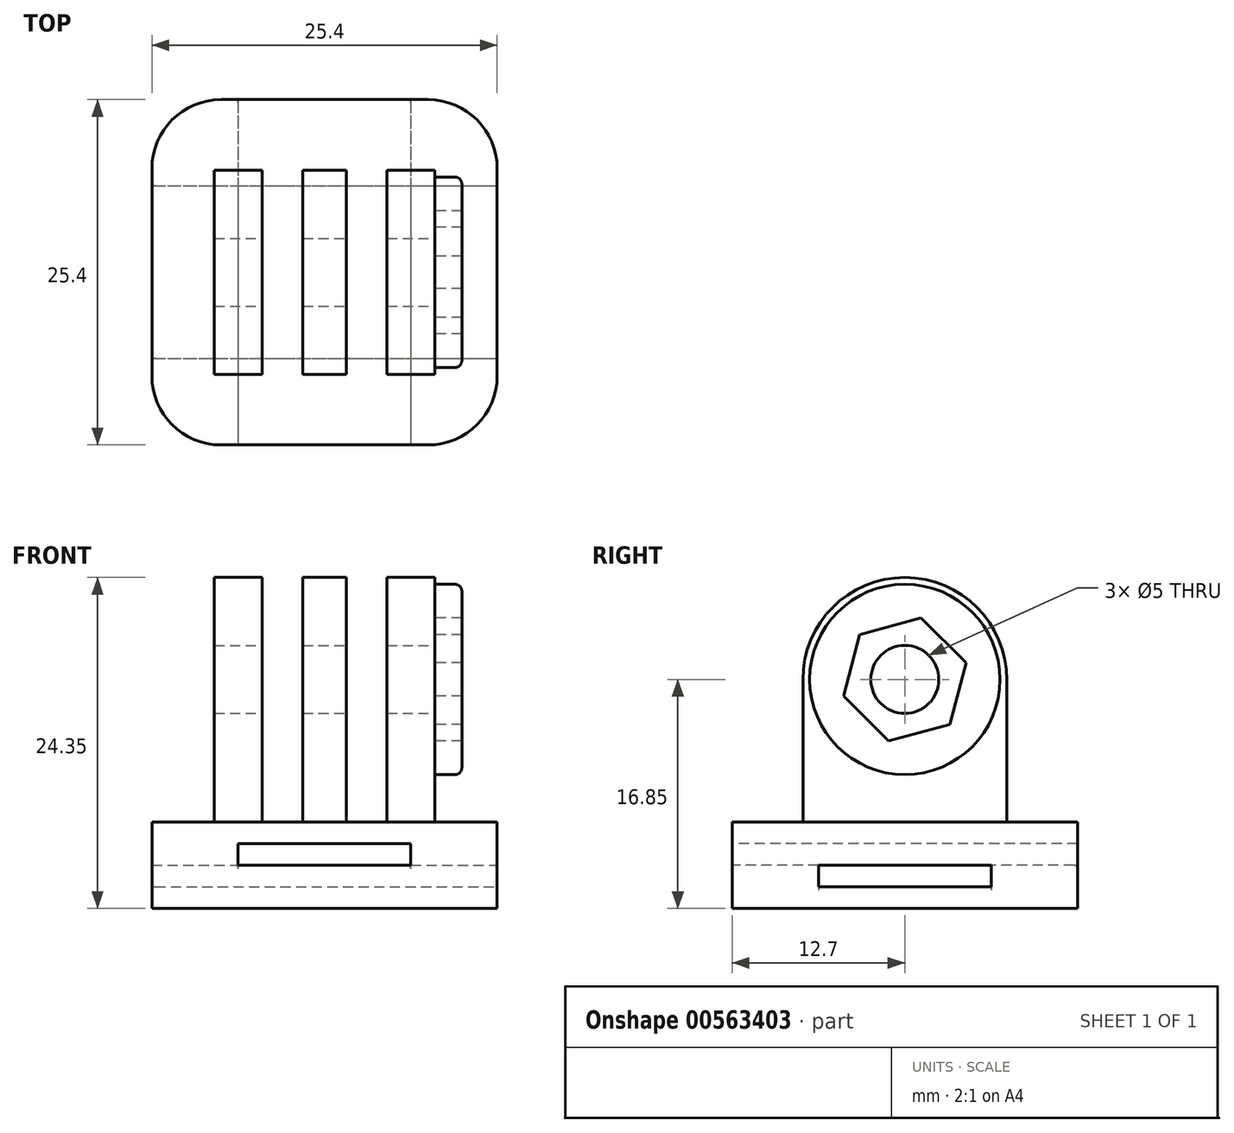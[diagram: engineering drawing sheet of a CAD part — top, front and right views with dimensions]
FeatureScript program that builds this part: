
annotation { "Feature Type Name" : "Feature", "Feature Type Description" : "" }
export const myFeature = defineFeature(function(context is Context, id is Id, definition is map)
    precondition{}
    {
        {
            var Q0;
            Q0=qCreatedBy(makeId("Top.planeOp"),FACE);
            var sketch = newSketch(context, id + "F0", { "sketchPlane" : qUnion([Q0])});
            skLineSegment(sketch, "E0.bottom", {"start": v(-12.7, 12.7) * mm, "end": v(12.7, 12.7) * mm});
            skLineSegment(sketch, "E0.top", {"start": v(-12.7, -12.7) * mm, "end": v(12.7, -12.7) * mm});
            skLineSegment(sketch, "E0.left", {"start": v(-12.7, 12.7) * mm, "end": v(-12.7, -12.7) * mm});
            skLineSegment(sketch, "E0.right", {"start": v(12.7, 12.7) * mm, "end": v(12.7, -12.7) * mm});
            skPoint(sketch, "E0.middle", {"position": v(0, 0) * mm});
            skSolve(sketch);
        }
        {
            var Q0;
            Q0=makeQuery(id+"F0.imprint","IMPRINT",FACE,{"disambiguationData":[TD([[makeQuery(id+"F0.imprint","IMPRINT",EDGE,{"derivedFrom":sQuery(id+"F0.wireOp",EDGE,"E0.bottom")}),-1.0]])]});
            extrude(context, id + "F1", {"entities" : qUnion([Q0]), "depth" : 6.35 * mm, "offsetDistance" : 25.4 * mm});
        }
        {
            var Q0;
            Q0=makeQuery(id+"F1.opExtrude","SWEPT_FACE",FACE,{"disambiguationData":[OSD([sQuery(id+"F0.wireOp",EDGE,"E0.right")])]});
            var sketch = newSketch(context, id + "F2", { "sketchPlane" : qUnion([Q0])});
            skLineSegment(sketch, "E1.bottom", {"start": v(-6.35, 3.17) * mm, "end": v(6.35, 3.18) * mm});
            skLineSegment(sketch, "E1.top", {"start": v(-6.35, 1.59) * mm, "end": v(6.35, 1.59) * mm});
            skLineSegment(sketch, "E1.left", {"start": v(-6.35, 3.17) * mm, "end": v(-6.35, 1.59) * mm});
            skLineSegment(sketch, "E1.right", {"start": v(6.35, 3.18) * mm, "end": v(6.35, 1.59) * mm});
            skPoint(sketch, "E1.middle", {"position": v(0, 2.38) * mm});
            skSolve(sketch);
        }
        {
            var Q0;
            Q0=makeQuery(id+"F2.imprint","IMPRINT",FACE,{"disambiguationData":[TD([[makeQuery(id+"F2.imprint","IMPRINT",EDGE,{"derivedFrom":sQuery(id+"F2.wireOp",EDGE,"E1.bottom")}),-1.0]])]});
            extrude(context, id + "F3", {"entities" : qUnion([Q0]), "operationType" : NewBodyOperationType.REMOVE, "endBound" : BoundingType.THROUGH_ALL, "oppositeDirection" : true, "depth" : 25.4 * mm, "offsetDistance" : 25.4 * mm});
        }
        {
            var Q0;
            Q0=makeQuery(id+"F1.opExtrude","SWEPT_FACE",FACE,{"disambiguationData":[OSD([sQuery(id+"F0.wireOp",EDGE,"E0.top")])]});
            var sketch = newSketch(context, id + "F4", { "sketchPlane" : qUnion([Q0])});
            skLineSegment(sketch, "E2.bottom", {"start": v(-6.35, 4.76) * mm, "end": v(6.35, 4.76) * mm});
            skLineSegment(sketch, "E2.top", {"start": v(-6.35, 3.17) * mm, "end": v(6.35, 3.17) * mm});
            skLineSegment(sketch, "E2.left", {"start": v(-6.35, 4.76) * mm, "end": v(-6.35, 3.17) * mm});
            skLineSegment(sketch, "E2.right", {"start": v(6.35, 4.76) * mm, "end": v(6.35, 3.17) * mm});
            skPoint(sketch, "E2.middle", {"position": v(0, 3.97) * mm});
            skSolve(sketch);
        }
        {
            var Q0;
            Q0=makeQuery(id+"F4.imprint","IMPRINT",FACE,{"disambiguationData":[TD([[makeQuery(id+"F4.imprint","IMPRINT",EDGE,{"derivedFrom":sQuery(id+"F4.wireOp",EDGE,"E2.bottom")}),-1.0]])]});
            extrude(context, id + "F5", {"entities" : qUnion([Q0]), "operationType" : NewBodyOperationType.REMOVE, "endBound" : BoundingType.THROUGH_ALL, "oppositeDirection" : true, "depth" : 25.4 * mm, "offsetDistance" : 25.4 * mm});
        }
        {
            var Q0;
            Q0=makeQuery(id+"F1.opExtrude","CAP_FACE",FACE,{"disambiguationData":[OSD([sQuery(id+"F0.wireOp",EDGE,"E0.bottom"),sQuery(id+"F0.wireOp",EDGE,"E0.top"),sQuery(id+"F0.wireOp",EDGE,"E0.left"),sQuery(id+"F0.wireOp",EDGE,"E0.right")])],"isStart":false});
            var sketch = newSketch(context, id + "F6", { "sketchPlane" : qUnion([Q0])});
            skLineSegment(sketch, "E3.bottom", {"start": v(-1.6, 7.5) * mm, "end": v(1.6, 7.5) * mm});
            skLineSegment(sketch, "E3.top", {"start": v(-1.6, -7.5) * mm, "end": v(1.6, -7.5) * mm});
            skLineSegment(sketch, "E3.left", {"start": v(-1.6, 7.5) * mm, "end": v(-1.6, -7.5) * mm});
            skLineSegment(sketch, "E3.right", {"start": v(1.6, 7.5) * mm, "end": v(1.6, -7.5) * mm});
            skPoint(sketch, "E3.middle", {"position": v(0, 0) * mm});
            skLineSegment(sketch, "E4.bottom", {"start": v(4.6, 7.5) * mm, "end": v(8.1, 7.5) * mm});
            skLineSegment(sketch, "E4.top", {"start": v(4.6, -7.5) * mm, "end": v(8.1, -7.5) * mm});
            skLineSegment(sketch, "E4.left", {"start": v(4.6, 7.5) * mm, "end": v(4.6, -7.5) * mm});
            skLineSegment(sketch, "E4.right", {"start": v(8.1, 7.5) * mm, "end": v(8.1, -7.5) * mm});
            skPoint(sketch, "E4.middle", {"position": v(6.35, 0) * mm});
            skLineSegment(sketch, "E5.MirrorCS", {"start": v(-4.6, 7.5) * mm, "end": v(-4.6, -7.5) * mm});
            skLineSegment(sketch, "E6.MirrorCS", {"start": v(-4.6, 7.5) * mm, "end": v(-8.1, 7.5) * mm});
            skLineSegment(sketch, "E7.MirrorCS", {"start": v(-8.1, 7.5) * mm, "end": v(-8.1, -7.5) * mm});
            skLineSegment(sketch, "E8.MirrorCS", {"start": v(-4.6, -7.5) * mm, "end": v(-8.1, -7.5) * mm});
            skSolve(sketch);
        }
        {
            var Q0;
            Q0=makeQuery(id+"F6.imprint","IMPRINT",FACE,{"disambiguationData":[TD([[makeQuery(id+"F6.imprint","IMPRINT",EDGE,{"derivedFrom":sQuery(id+"F6.wireOp",EDGE,"E5.MirrorCS")}),-1.0]])]});
            var Q1;
            Q1=makeQuery(id+"F6.imprint","IMPRINT",FACE,{"disambiguationData":[TD([[makeQuery(id+"F6.imprint","IMPRINT",EDGE,{"derivedFrom":sQuery(id+"F6.wireOp",EDGE,"E3.bottom")}),-1.0]])]});
            var Q2;
            Q2=makeQuery(id+"F6.imprint","IMPRINT",FACE,{"disambiguationData":[TD([[makeQuery(id+"F6.imprint","IMPRINT",EDGE,{"derivedFrom":sQuery(id+"F6.wireOp",EDGE,"E4.bottom")}),-1.0]])]});
            extrude(context, id + "F7", {"entities" : qUnion([Q0, Q1, Q2]), "operationType" : NewBodyOperationType.ADD, "depth" : 18 * mm, "offsetDistance" : 25.4 * mm});
        }
        {
            var Q0;
            Q0=makeQuery(id+"F7.opExtrude","CAP_EDGE",EDGE,{"disambiguationData":[OSD([sQuery(id+"F6.wireOp",EDGE,"E4.top")])],"isStart":false});
            var Q1;
            Q1=makeQuery(id+"F7.opExtrude","CAP_EDGE",EDGE,{"disambiguationData":[OSD([sQuery(id+"F6.wireOp",EDGE,"E3.top")])],"isStart":false});
            var Q2;
            Q2=makeQuery(id+"F7.opExtrude","CAP_EDGE",EDGE,{"disambiguationData":[OSD([sQuery(id+"F6.wireOp",EDGE,"E8.MirrorCS")])],"isStart":false});
            var Q3;
            Q3=makeQuery(id+"F7.opExtrude","CAP_EDGE",EDGE,{"disambiguationData":[OSD([sQuery(id+"F6.wireOp",EDGE,"E6.MirrorCS")])],"isStart":false});
            var Q4;
            Q4=makeQuery(id+"F7.opExtrude","CAP_EDGE",EDGE,{"disambiguationData":[OSD([sQuery(id+"F6.wireOp",EDGE,"E4.bottom")])],"isStart":false});
            var Q5;
            Q5=makeQuery(id+"F7.opExtrude","CAP_EDGE",EDGE,{"disambiguationData":[OSD([sQuery(id+"F6.wireOp",EDGE,"E3.bottom")])],"isStart":false});
            fillet(context, id + "F8", {"entities" : qUnion([Q0, Q1, Q2, Q3, Q4, Q5]), "radius" : 7.5 * mm, "tangentPropagation" : true, "allowEdgeOverflow" : false});
        }
        {
            var Q0;
            Q0=makeQuery(id+"F1.opExtrude","SWEPT_EDGE",EDGE,{"disambiguationData":[OSD([sQuery(id+"F0.wireOp",EDGE,"E0.bottom"),sQuery(id+"F0.wireOp",EDGE,"E0.right")])]});
            var Q1;
            Q1=makeQuery(id+"F1.opExtrude","SWEPT_EDGE",EDGE,{"disambiguationData":[OSD([sQuery(id+"F0.wireOp",EDGE,"E0.top"),sQuery(id+"F0.wireOp",EDGE,"E0.right")])]});
            var Q2;
            Q2=makeQuery(id+"F1.opExtrude","SWEPT_EDGE",EDGE,{"disambiguationData":[OSD([sQuery(id+"F0.wireOp",EDGE,"E0.bottom"),sQuery(id+"F0.wireOp",EDGE,"E0.left")])]});
            var Q3;
            Q3=makeQuery(id+"F1.opExtrude","SWEPT_EDGE",EDGE,{"disambiguationData":[OSD([sQuery(id+"F0.wireOp",EDGE,"E0.top"),sQuery(id+"F0.wireOp",EDGE,"E0.left")])]});
            fillet(context, id + "F9", {"entities" : qUnion([Q0, Q1, Q2, Q3]), "radius" : 5.08 * mm, "tangentPropagation" : true, "allowEdgeOverflow" : false});
        }
        {
            var Q0;
            Q0=makeQuery(id+"F7.opExtrude","SWEPT_FACE",FACE,{"disambiguationData":[OSD([sQuery(id+"F6.wireOp",EDGE,"E4.right")])]});
            var sketch = newSketch(context, id + "F10", { "sketchPlane" : qUnion([Q0])});
            skPoint(sketch, "E9", {"position": v(0, 16.85) * mm});
            skCircle(sketch, "E10.cCircle", {"center": v(0, 16.85) * mm, "radius": 4.68 * mm, "construction": true});
            skLineSegment(sketch, "E10.0", {"start": v(-3.32, 20.15) * mm, "end": v(1.2, 21.37) * mm});
            skLineSegment(sketch, "E10.1", {"start": v(1.2, 21.37) * mm, "end": v(4.51, 18.07) * mm});
            skLineSegment(sketch, "E10.2", {"start": v(4.51, 18.07) * mm, "end": v(3.32, 13.55) * mm});
            skLineSegment(sketch, "E10.3", {"start": v(3.32, 13.55) * mm, "end": v(-1.2, 12.33) * mm});
            skLineSegment(sketch, "E10.4", {"start": v(-1.2, 12.33) * mm, "end": v(-4.51, 15.63) * mm});
            skLineSegment(sketch, "E10.5", {"start": v(-4.51, 15.63) * mm, "end": v(-3.32, 20.15) * mm});
            skCircle(sketch, "E11", {"center": v(0, 16.85) * mm, "radius": 7 * mm});
            skSolve(sketch);
        }
        {
            var Q0;
            Q0=makeQuery(id+"F10.imprint","IMPRINT",FACE,{"disambiguationData":[TD([[makeQuery(id+"F10.imprint","IMPRINT",EDGE,{"derivedFrom":sQuery(id+"F10.wireOp",EDGE,"E10.0")}),1.0]])]});
            extrude(context, id + "F11", {"entities" : qUnion([Q0]), "operationType" : NewBodyOperationType.ADD, "depth" : 2 * mm, "offsetDistance" : 25.4 * mm});
        }
        {
            var Q0;
            Q0=sQuery(id+"F10.wireOp",VERTEX,"E9");
            var Q1;
            Q1=makeQuery(id+"F1.opExtrude","SWEPT_BODY",BODY,{"disambiguationData":[OSD([sQuery(id+"F0.wireOp",EDGE,"E0.bottom"),sQuery(id+"F0.wireOp",EDGE,"E0.top"),sQuery(id+"F0.wireOp",EDGE,"E0.left"),sQuery(id+"F0.wireOp",EDGE,"E0.right")])]});
            hole(context, id + "F12", {"style" : HoleStyle.SIMPLE, "endStyle" : HoleEndStyle.THROUGH, "holeDiameter" : 5 * mm, "majorDiameter" : 6.35 * mm, "isTappedThrough" : true, "tappedDepth" : 12.7 * mm, "tapClearance" : 3, "locations" : qUnion([Q0]), "scope" : qUnion([Q1])});
        }
        {
            var Q0;
            Q0=makeQuery(id+"F11.opExtrude","CAP_EDGE",EDGE,{"disambiguationData":[OSD([sQuery(id+"F10.wireOp",EDGE,"E11")])],"isStart":false});
            fillet(context, id + "F13", {"entities" : qUnion([Q0]), "radius" : 0.5 * mm, "tangentPropagation" : true, "allowEdgeOverflow" : false});
        }
        {
            var Q0;
            Q0=makeQuery(id+"F3.boolean.opBoolean","INTERSECT",EDGE,{"derivedFrom":[makeQuery(id+"F1.opExtrude","SWEPT_FACE",FACE,{"disambiguationData":[OSD([sQuery(id+"F0.wireOp",EDGE,"E0.left")])]}),makeQuery(id+"F3.opExtrude","SWEPT_FACE",FACE,{"disambiguationData":[OSD([sQuery(id+"F2.wireOp",EDGE,"E1.top")])]})]});
            var Q1;
            Q1=makeQuery(id+"F5.boolean.opBoolean","COPY",EDGE,{"derivedFrom":makeQuery(id+"F5.opExtrude","CAP_EDGE",EDGE,{"disambiguationData":[OSD([sQuery(id+"F4.wireOp",EDGE,"E2.top")])],"isStart":true})});
            var Q2;
            Q2=makeQuery(id+"F3.boolean.opBoolean","COPY",EDGE,{"derivedFrom":makeQuery(id+"F3.opExtrude","CAP_EDGE",EDGE,{"disambiguationData":[OSD([sQuery(id+"F2.wireOp",EDGE,"E1.top")])],"isStart":true})});
            var Q3;
            Q3=makeQuery(id+"F5.boolean.opBoolean","INTERSECT",EDGE,{"derivedFrom":[makeQuery(id+"F1.opExtrude","SWEPT_FACE",FACE,{"disambiguationData":[OSD([sQuery(id+"F0.wireOp",EDGE,"E0.bottom")])]}),makeQuery(id+"F5.opExtrude","SWEPT_FACE",FACE,{"disambiguationData":[OSD([sQuery(id+"F4.wireOp",EDGE,"E2.top")])]})]});
            fillet(context, id + "F14", {"entities" : qUnion([Q0, Q1, Q2, Q3]), "radius" : 0.25 * mm, "tangentPropagation" : true, "allowEdgeOverflow" : false});
        }
    });
